# Revit family: 3502A_NX_In_Fiture_Module_Inline
name_source: partatom
category: Communication Devices
revit_build: Autodesk Revit 2014 (Build: 20130308_1515(x64)
units: mm (PartAtom-declared; Revit-internal decimal feet)

## types (1)
- 3502A_NX_In_Fiture_Module_Inline
    Apparent Load = 0 VA
    Assembly Code = D5090
    Certifications = Conforms with UL916 and Certified to CAN/CSA C22.2 No. 205-M1983
IC Approved
    Default Elevation = 48 "
    Description = It enables a complete control solution for a single luminaire
    Electrical Rating = Input: 120-347VAC, 10A Max, 50-60Hz
Output: 10A, 120VAC only Incandescent
 10A, 120-347VAC, Magnetic Ballast
 5A, 120-277VAC, Electronic Ballast
 3A, 347VAC, Electronic Ballast
Surge Withstand: 2000V
Peak Inrush: 160A for 2 ms Max
    Features = Designed for installation within luminaire housing
• Universal Voltage, 120 - 347V
• Space saving in-line flying leads, connector and mounting tabs
• Integral relay for On/Off control
• Continuous dimming 0 - 10V
• Second dimming channel for variable color temperature
• Compatible with SpectraSync™ enabled luminaires
• Wireless programming via free Smart Device App*
• Create and download schedules via Smart Device App*
• SmartPORT™ technology for plug-in control and radio options
• Suitable for indoor and outdoor applications
• 5 year limited warranty
    Housing Material = Metal-Hubbell-Aluminum Anodized Blue
    Manufacturer = Hubbell Control Solutions
    Model = NXFM series in-fixture module
    Product Documentation Link = https://hubbellcdn.com
    Product Page URL = https://www.hubbell.com
    Sensing Element = Paint - Hubbell - Carbon Black
    Type Comments = In-Fixture Module- Inline
    URL = https://www.hubbell.com
    Voltage = 120 V
    Warranty = 5-Years Warranty

## geometry (parser evidence)
native form markers: Sweep x1
no freeform markers — native parametric forms only
